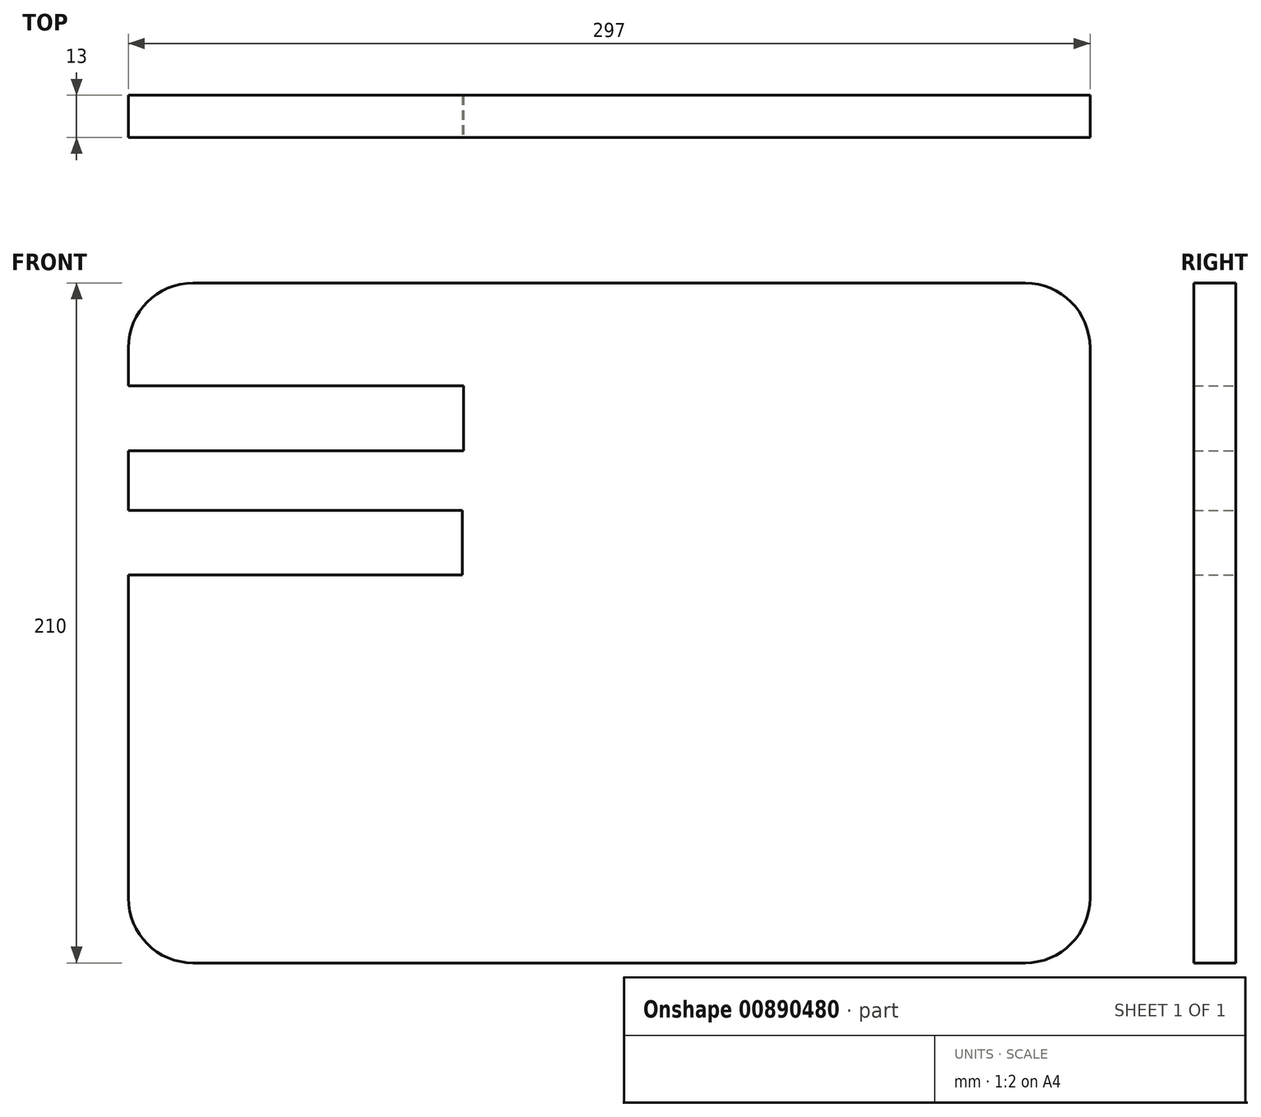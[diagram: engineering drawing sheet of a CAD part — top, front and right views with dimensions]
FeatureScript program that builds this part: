
annotation { "Feature Type Name" : "Feature", "Feature Type Description" : "" }
export const myFeature = defineFeature(function(context is Context, id is Id, definition is map)
    precondition{}
    {
        {
            var Q0;
            Q0=qCreatedBy(makeId("Front.planeOp"),FACE);
            var sketch = newSketch(context, id + "F0", { "sketchPlane" : qUnion([Q0])});
            skLineSegment(sketch, "E0.bottom", {"start": v(-38.2, 176.44) * mm, "end": v(218.8, 176.44) * mm});
            skLineSegment(sketch, "E0.top", {"start": v(-38.2, -33.56) * mm, "end": v(218.8, -33.56) * mm});
            skLineSegment(sketch, "E0.left", {"start": v(-58.2, 156.44) * mm, "end": v(-58.2, -13.56) * mm});
            skLineSegment(sketch, "E0.right", {"start": v(238.8, 156.44) * mm, "end": v(238.8, -13.56) * mm});
            skPoint(sketch, "E1.visualSharp", {"position": v(-58.2, 176.44) * mm});
            skArc(sketch, "E1.filletArc", {"start": v(-38.2, 176.44) * mm, "mid": v(-52.34, 170.58) * mm, "end": v(-58.2, 156.44) * mm});
            skPoint(sketch, "E2.visualSharp", {"position": v(238.8, 176.44) * mm});
            skArc(sketch, "E2.filletArc", {"start": v(238.8, 156.44) * mm, "mid": v(232.94, 170.58) * mm, "end": v(218.8, 176.44) * mm});
            skPoint(sketch, "E3.visualSharp", {"position": v(238.8, -33.56) * mm});
            skArc(sketch, "E3.filletArc", {"start": v(218.8, -33.56) * mm, "mid": v(232.94, -27.7) * mm, "end": v(238.8, -13.56) * mm});
            skPoint(sketch, "E4.visualSharp", {"position": v(-58.2, -33.56) * mm});
            skArc(sketch, "E4.filletArc", {"start": v(-58.2, -13.56) * mm, "mid": v(-52.34, -27.7) * mm, "end": v(-38.2, -33.56) * mm});
            skSolve(sketch);
        }
        {
            var Q0;
            Q0 = qSketchRegion(id + "F0", true);
            extrude(context, id + "F1", {"entities" : qUnion([Q0]), "depth" : 13 * mm, "offsetDistance" : 25 * mm});
        }
        {
            var Q0;
            Q0=makeQuery(id+"F1.opExtrude","CAP_FACE",FACE,{"disambiguationData":[OSD([sQuery(id+"F0.wireOp",EDGE,"E0.bottom"),sQuery(id+"F0.wireOp",EDGE,"E0.top"),sQuery(id+"F0.wireOp",EDGE,"E0.left"),sQuery(id+"F0.wireOp",EDGE,"E0.right"),sQuery(id+"F0.wireOp",EDGE,"E1.filletArc"),sQuery(id+"F0.wireOp",EDGE,"E2.filletArc"),sQuery(id+"F0.wireOp",EDGE,"E3.filletArc"),sQuery(id+"F0.wireOp",EDGE,"E4.filletArc")])],"isStart":false});
            var sketch = newSketch(context, id + "F2", { "sketchPlane" : qUnion([Q0])});
            skLineSegment(sketch, "E5.bottom", {"start": v(-64.65, 124.68) * mm, "end": v(45.35, 124.68) * mm});
            skLineSegment(sketch, "E5.top", {"start": v(-64.65, 144.68) * mm, "end": v(45.35, 144.68) * mm});
            skLineSegment(sketch, "E5.left", {"start": v(-64.65, 124.68) * mm, "end": v(-64.65, 144.68) * mm});
            skLineSegment(sketch, "E5.right", {"start": v(45.35, 124.68) * mm, "end": v(45.35, 144.68) * mm});
            skSolve(sketch);
        }
        {
            var Q0;
            Q0 = qSketchRegion(id + "F2", true);
            extrude(context, id + "F3", {"entities" : qUnion([Q0]), "operationType" : NewBodyOperationType.REMOVE, "oppositeDirection" : true, "depth" : 25 * mm, "offsetDistance" : 25 * mm});
        }
        {
            var Q0;
            Q0=makeQuery(id+"F1.opExtrude","CAP_FACE",FACE,{"disambiguationData":[OSD([sQuery(id+"F0.wireOp",EDGE,"E0.bottom"),sQuery(id+"F0.wireOp",EDGE,"E0.top"),sQuery(id+"F0.wireOp",EDGE,"E0.left"),sQuery(id+"F0.wireOp",EDGE,"E0.right"),sQuery(id+"F0.wireOp",EDGE,"E1.filletArc"),sQuery(id+"F0.wireOp",EDGE,"E2.filletArc"),sQuery(id+"F0.wireOp",EDGE,"E3.filletArc"),sQuery(id+"F0.wireOp",EDGE,"E4.filletArc")])],"isStart":false});
            var sketch = newSketch(context, id + "F4", { "sketchPlane" : qUnion([Q0])});
            skLineSegment(sketch, "E6.bottom", {"start": v(-65.07, 86.25) * mm, "end": v(44.93, 86.25) * mm});
            skLineSegment(sketch, "E6.top", {"start": v(-65.07, 106.25) * mm, "end": v(44.93, 106.25) * mm});
            skLineSegment(sketch, "E6.left", {"start": v(-65.07, 86.25) * mm, "end": v(-65.07, 106.25) * mm});
            skLineSegment(sketch, "E6.right", {"start": v(44.93, 86.25) * mm, "end": v(44.93, 106.25) * mm});
            skSolve(sketch);
        }
        {
            var Q0;
            Q0 = qSketchRegion(id + "F4", true);
            extrude(context, id + "F5", {"entities" : qUnion([Q0]), "operationType" : NewBodyOperationType.REMOVE, "oppositeDirection" : true, "depth" : 25 * mm, "offsetDistance" : 25 * mm});
        }
    });
